# Revit family: Power-ModularDevices-GEWISS-90AM-SWITCH_DISCONNECTOR_1P
name_source: partatom
category: Apparecchi elettrici
revit_build: Autodesk Revit 2016 (Build: 20161004_0715(x64)
units: mm (PartAtom-declared; Revit-internal decimal feet)

## family parameters
Condiviso = No
Host = Superficie
Mantenere orientamento annotazione = Sì
Numero OmniClass = 23.80.50.00
Punto di calcolo locali = Sì
Quota connettore circolare = Usa diametro
Taglio con vuoti quando caricato = No
Tipo di parte = Normale
Titolo OmniClass = Terminals for Power Supply

## types (6) — shared parameters
Catalogue = POWER
Catalogue Range = 90 AM
Electrocod = 1422
IDF = 5e9ca414-9624-4947-b1af-397c8127a2ce
IDT = 40516cf6-468f-4aee-98f1-bc95d749a16b
Immagine tipo = GW96149.jpg
No. Chorus modules = 1
No. of modules EN 50022 = 1
No. of poles = 1P
Number of poles = 1P
Numero di poli_ = 1
Produttore = GEWISS S.p.A.
Prospetto di default = 1219 mm
Rated voltage = 240Vac
Rated voltage AC = 240V
SEO = Disconnector
Spostamento_x = -340 mm
Standard = EN 60947-3
Technical sheet = https://www.gewiss.com
URL = https://www.gewiss.com
Version file RFA = 18.0
carico = Altro
potenza in watt = 0 V
zero-valued in all types: Barra_DIN

## per-type parameters (varying)
| type | Descrizione | EAN code | Modello | Rated current (In) | Rated current: |
| GW96149 - SWITCH DISCONNECTOR 1P 125A | SWITCH DISCONNECTOR 1P 125A | 8011564131644 | GW96149 | 125A | 125A |
| GW96105 - SWITCH DISCONNECTOR 1P 40A | SWITCH DISCONNECTOR 1P 40A | 8011564113695 | GW96105 | 40A | 40A |
| GW96147 - SWITCH DISCONNECTOR 1P 80A | SWITCH DISCONNECTOR 1P 80A | 8011564131620 | GW96147 | 80A | 80A |
| GW96146 - SWITCH DISCONNECTOR 1P 63A | SWITCH DISCONNECTOR 1P 63A | 8011564131613 | GW96146 | 63A | 63A |
| GW96148 - SWITCH DISCONNECTOR 1P 100A | SWITCH DISCONNECTOR 1P 100A | 8011564131637 | GW96148 | 100A | 100A |
| GW96104 - SWITCH DISCONNECTOR 1P 32A | SWITCH DISCONNECTOR 1P 32A | 8011564110250 | GW96104 | 32A | 32A |
